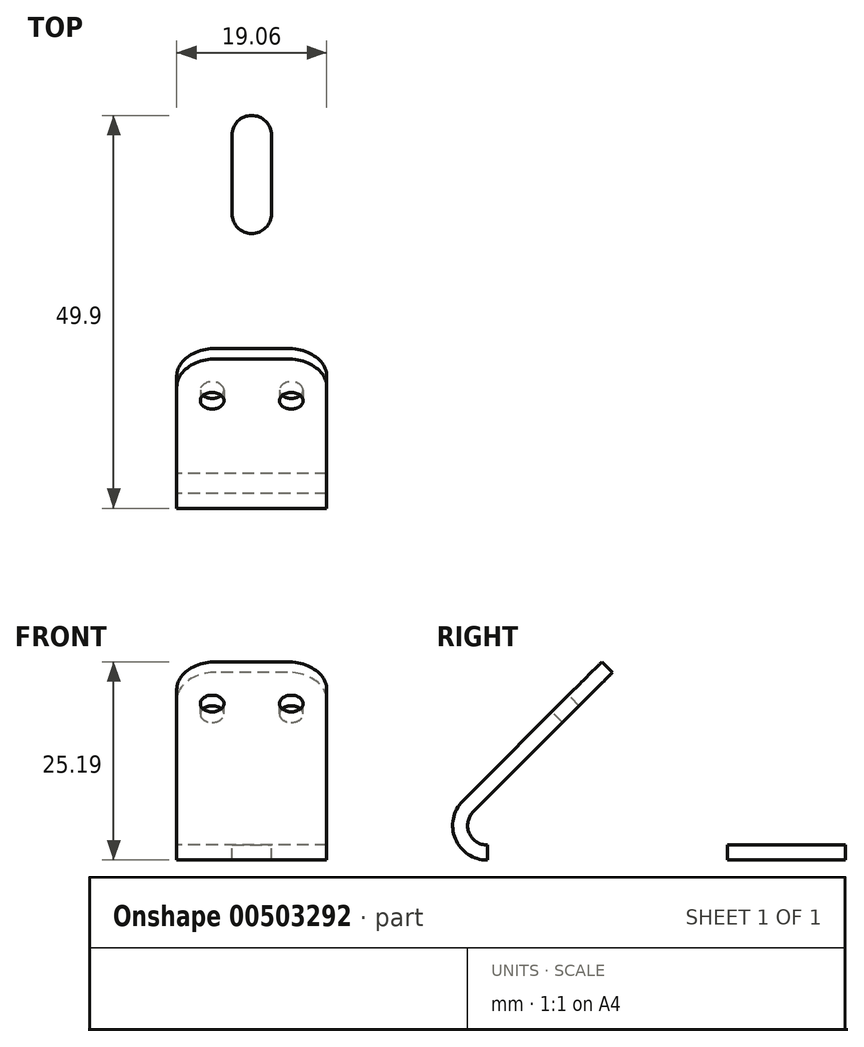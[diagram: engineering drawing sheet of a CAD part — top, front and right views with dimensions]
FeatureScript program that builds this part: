
annotation { "Feature Type Name" : "Feature", "Feature Type Description" : "" }
export const myFeature = defineFeature(function(context is Context, id is Id, definition is map)
    precondition{}
    {
        {
            var Q0;
            Q0=qCreatedBy(makeId("Right.planeOp"),FACE);
            var sketch = newSketch(context, id + "F0", { "sketchPlane" : qUnion([Q0])});
            skArc(sketch, "E0", {"start": v(-3.11, 3.11) * mm, "mid": v(-4.07, -1.68) * mm, "end": v(0, -4.4) * mm});
            skLineSegment(sketch, "E1", {"start": v(-3.11, 3.11) * mm, "end": v(14.57, 20.79) * mm});
            skLineSegment(sketch, "E2", {"start": v(0, -4.4) * mm, "end": v(50, -4.4) * mm});
            skLineSegment(sketch, "E3.0", {"start": v(-1.77, 1.77) * mm, "end": v(15.9, 19.45) * mm});
            skArc(sketch, "E3.1", {"start": v(-1.77, 1.77) * mm, "mid": v(-2.3, -0.96) * mm, "end": v(0, -2.5) * mm});
            skLineSegment(sketch, "E3.2", {"start": v(0, -2.5) * mm, "end": v(50, -2.5) * mm});
            skLineSegment(sketch, "E4", {"start": v(15.9, 19.45) * mm, "end": v(14.57, 20.79) * mm});
            skLineSegment(sketch, "E5", {"start": v(50, -4.4) * mm, "end": v(50, -2.5) * mm});
            skSolve(sketch);
        }
        {
            var Q0;
            Q0=makeQuery(id+"F0.imprint","IMPRINT",FACE,{"disambiguationData":[TD([[makeQuery(id+"F0.imprint","IMPRINT",EDGE,{"derivedFrom":sQuery(id+"F0.wireOp",EDGE,"E0")}),1.0]])]});
            extrude(context, id + "F1", {"entities" : qUnion([Q0]), "endBound" : BoundingType.SYMMETRIC, "depth" : 19.05 * mm});
        }
        {
            var Q0;
            Q0=makeQuery(id+"F1.opExtrude","SWEPT_FACE",FACE,{"disambiguationData":[OSD([sQuery(id+"F0.wireOp",EDGE,"E1")])]});
            var sketch = newSketch(context, id + "F2", { "sketchPlane" : qUnion([Q0])});
            skCircle(sketch, "E6", {"center": v(-5.03, 17.5) * mm, "radius": 1.5 * mm});
            skCircle(sketch, "E7", {"center": v(5.03, 17.5) * mm, "radius": 1.5 * mm});
            skSolve(sketch);
        }
        {
            var Q0;
            Q0=makeQuery(id+"F2.imprint","IMPRINT",FACE,{"disambiguationData":[TD([[makeQuery(id+"F2.imprint","IMPRINT",EDGE,{"derivedFrom":sQuery(id+"F2.wireOp",EDGE,"E6")}),1.0]])]});
            var Q1;
            Q1=makeQuery(id+"F2.imprint","IMPRINT",FACE,{"disambiguationData":[TD([[makeQuery(id+"F2.imprint","IMPRINT",EDGE,{"derivedFrom":sQuery(id+"F2.wireOp",EDGE,"E7")}),1.0]])]});
            var Q2;
            Q2=makeQuery(id+"F1.opExtrude","SWEPT_FACE",FACE,{"disambiguationData":[OSD([sQuery(id+"F0.wireOp",EDGE,"E3.0")])]});
            extrude(context, id + "F3", {"entities" : qUnion([Q0, Q1]), "operationType" : NewBodyOperationType.REMOVE, "endBound" : BoundingType.UP_TO_SURFACE, "oppositeDirection" : true, "endBoundEntityFace" : qUnion([Q2]), "depth" : 25 * mm});
        }
        {
            var Q0;
            Q0=makeQuery(id+"F1.opExtrude","SWEPT_FACE",FACE,{"disambiguationData":[OSD([sQuery(id+"F0.wireOp",EDGE,"E3.2")])]});
            var sketch = newSketch(context, id + "F4", { "sketchPlane" : qUnion([Q0])});
            skLineSegment(sketch, "E8", {"start": v(0, 33) * mm, "end": v(0, 43) * mm, "construction": true});
            skCircle(sketch, "E9", {"center": v(0, 18) * mm, "radius": 2.5 * mm});
            skArc(sketch, "E10.0.startCap", {"start": v(2.5, 33) * mm, "mid": v(0, 30.5) * mm, "end": v(-2.5, 33) * mm});
            skArc(sketch, "E10.0.endCap", {"start": v(-2.5, 43) * mm, "mid": v(0, 45.5) * mm, "end": v(2.5, 43) * mm});
            skLineSegment(sketch, "E10.0.left", {"start": v(-2.5, 33) * mm, "end": v(-2.5, 43) * mm});
            skLineSegment(sketch, "E10.0.right", {"start": v(2.5, 33) * mm, "end": v(2.5, 43) * mm});
            skSolve(sketch);
        }
        {
            var Q0;
            Q0=makeQuery(id+"F4.imprint","IMPRINT",FACE,{"disambiguationData":[TD([[makeQuery(id+"F4.imprint","IMPRINT",EDGE,{"derivedFrom":sQuery(id+"F4.wireOp",EDGE,"E9")}),1.0]])]});
            var Q1;
            Q1=makeQuery(id+"F4.imprint","IMPRINT",FACE,{"disambiguationData":[TD([[makeQuery(id+"F4.imprint","IMPRINT",EDGE,{"derivedFrom":sQuery(id+"F4.wireOp",EDGE,"E10.0.startCap")}),-1.0]])]});
            var Q2;
            Q2=makeQuery(id+"F1.opExtrude","SWEPT_FACE",FACE,{"disambiguationData":[OSD([sQuery(id+"F0.wireOp",EDGE,"E2")])]});
            extrude(context, id + "F5", {"entities" : qUnion([Q0, Q1]), "operationType" : NewBodyOperationType.REMOVE, "endBound" : BoundingType.UP_TO_SURFACE, "oppositeDirection" : true, "endBoundEntityFace" : qUnion([Q2]), "depth" : 25 * mm});
        }
        {
            var Q0;
            Q0=makeQuery(id+"F1.opExtrude","CAP_EDGE",EDGE,{"disambiguationData":[OSD([sQuery(id+"F0.wireOp",EDGE,"E4")])],"isStart":false});
            var Q1;
            Q1=makeQuery(id+"F1.opExtrude","CAP_EDGE",EDGE,{"disambiguationData":[OSD([sQuery(id+"F0.wireOp",EDGE,"E4")])],"isStart":true});
            var Q2;
            Q2=makeQuery(id+"F1.opExtrude","CAP_EDGE",EDGE,{"disambiguationData":[OSD([sQuery(id+"F0.wireOp",EDGE,"E5")])],"isStart":true});
            var Q3;
            Q3=makeQuery(id+"F1.opExtrude","CAP_EDGE",EDGE,{"disambiguationData":[OSD([sQuery(id+"F0.wireOp",EDGE,"E5")])],"isStart":false});
            fillet(context, id + "F6", {"entities" : qUnion([Q0, Q1, Q2, Q3]), "radius" : 5 * mm, "tangentPropagation" : true, "allowEdgeOverflow" : false});
        }
    });
